# Revit family: Hager-Pedro-sistema-IT-it
name_source: partatom
category: Electrical Equipment
units: mm (PartAtom-declared; Revit-internal decimal feet)

## family parameters
Cut with Voids When Loaded = No
Host = Face
Panel Configuration = Two Columns, Circuits Across
Part Type = Panelboard
Room Calculation Point = No
Round Connector Dimension = Use Diameter
Shared = No

## types (12) — shared parameters
EF000003 - Tipo di montaggio = EV000384 - A parete
EF000007 - colore = EV000270 - grigio
EF000116 - numero RAL = 7035
EF000118 - con piastra di montaggio = No
EF000339 - tipo di copertura = EV004216 - porta
EF001062 - esecuzione EMC = Yes
EF001088 - possibilità di applicazione = Yes
EF001134 - barra DIN = Yes
EF001596 - Attacco Lampada = EV000139 - plastica
EF004462 - tipo di chiusura = EV000154 - altri
EF005474 - grado di protezione (IP) = EV006422 - IP66
EF006306 - con serratura = Yes
EF009212 - esecuzione coperchio = EV000116 - chiuso
EF015776 - Morsettiera di terra = No
EF015777 - Morsettiera neutra = No
EF015941 - Segnale di passaggio porta = No
HG000001 - Numero di colonne = 1
HG000002 - Con porta = Yes
HG000003 - Gamma = Pedro
HG000005 - Spessore = 3 mm  [stored 0.00984252 ft]
HG000006 - Ad incasso = No
HG000009 - Porta doppia a battente = No
HG000010 - Porte asimmetriche = No
HG000011 - File vuote nella parte basse = No
HG000017 - Distanza tra i poli = 18 mm  [stored 0.0590551 ft]
Manufacturer = Hager
Type Comments = Pedro
zero-valued in all types: Default Elevation, EF000218 - profondità di incasso, EF000332 - Altezza della parte incassata, EF000846 - larghezza di montaggio, HG000007 - Numero di colonne vuote, HG000008 - Numero di file vuote

## per-type parameters (varying)
| type | EF000008 - Larghezza | EF000040 - Altezza | EF000049 - profondità | EF000266 - numero di file | EF001131 - profondità interna | EF002950 - Numero moduli DIN | EF006244 - coperchio/porta trasparente | HG000004 - Codice produttore | Model |
| A parete IP66 L325 A428.2 P178 12 Unità di divisione - B04602 | 325 mm | 428 mm | 178 mm | 3 | 148 mm | 12 | No | B04602 | B04602 |
| A parete IP66 L325 A428.2 P178 12 Unità di divisione - B04622 | 325 mm | 428 mm | 178 mm | 3 | 148 mm | 12 | Yes | B04622 | B04622 |
| A parete IP66 L433.5 A503.7 P210 18 Unità di divisione - B04603 | 434 mm | 504 mm | 210 mm | 3 | 180 mm | 18 | No | B04603 | B04603 |
| A parete IP66 L433.5 A503.7 P210 18 Unità di divisione - B04623 | 434 mm | 504 mm | 210 mm | 3 | 180 mm | 18 | Yes | B04623 | B04623 |
| A parete IP66 L433.5 A653.6 P210 18 Unità di divisione - B04604 | 434 mm | 654 mm | 210 mm | 4 | 180 mm | 18 | No | B04604 | B04604 |
| A parete IP66 L433.5 A653.6 P210 18 Unità di divisione - B04624 | 434 mm | 654 mm | 210 mm | 4 | 180 mm | 18 | Yes | B04624 | B04624 |
| A parete IP66 L542.4 A654.6 P264.5 24 Unità di divisione - B04605 | 542 mm | 655 mm | 264 mm | 4 | 234 mm | 24 | No | B04605 | B04605 |
| A parete IP66 L542.4 A654.6 P264.5 24 Unità di divisione - B04625 | 542 mm | 655 mm | 264 mm | 4 | 234 mm | 24 | Yes | B04625 | B04625 |
| A parete IP66 L615.4 A805.6 P318.7 28 Unità di divisione - B04606 | 615 mm | 806 mm | 319 mm | 5 | 289 mm | 28 | No | B04606 | B04606 |
| A parete IP66 L615.4 A805.6 P318.7 28 Unità di divisione - B04626 | 615 mm | 806 mm | 319 mm | 5 | 289 mm | 28 | Yes | B04626 | B04626 |
| A parete IP66 L810 A1056.2 P355 38 Unità di divisione - B04608 | 810 mm | 1056 mm  [stored 3.46457 ft] | 355 mm | 5 | 319 mm | 38 | No | B04608 | B04608 |
| A parete IP66 L810 A1056.2 P355 38 Unità di divisione - B04628 | 810 mm | 1056 mm  [stored 3.46457 ft] | 355 mm | 5 | 319 mm | 38 | Yes | B04628 | B04628 |

note: [stored X ft] marks values corroborated as IEEE doubles in the binary element streams (Revit-internal decimal feet)

## geometry (parser evidence)
native form markers: Sweep x17
no freeform markers — native parametric forms only
